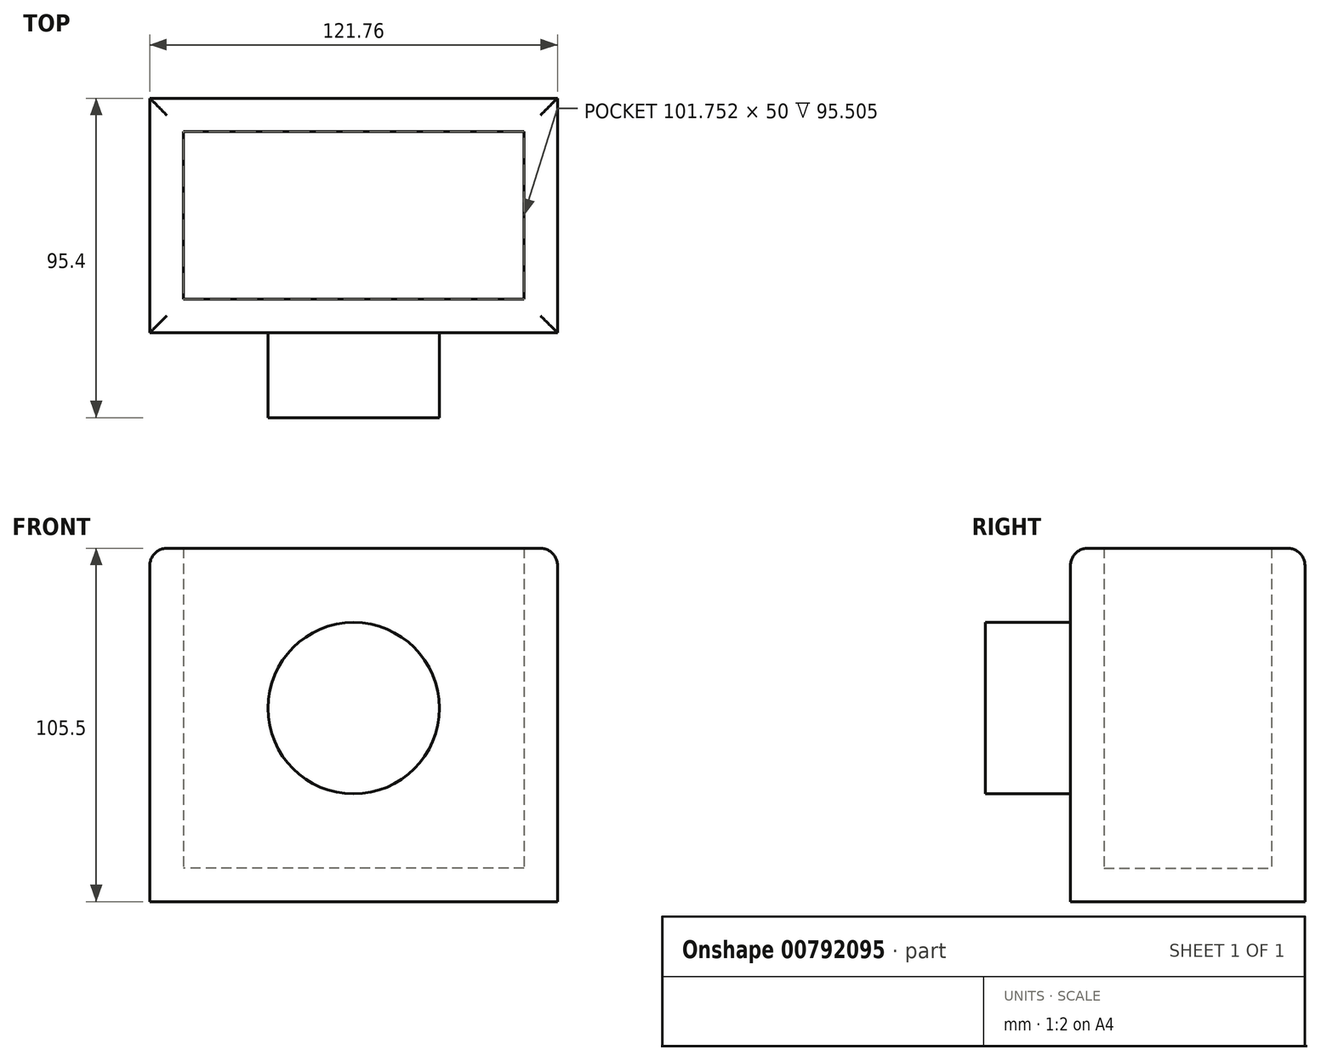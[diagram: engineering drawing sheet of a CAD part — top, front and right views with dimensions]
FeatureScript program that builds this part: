
annotation { "Feature Type Name" : "Feature", "Feature Type Description" : "" }
export const myFeature = defineFeature(function(context is Context, id is Id, definition is map)
    precondition{}
    {
        {
            var Q0;
            Q0=qCreatedBy(makeId("Front.planeOp"),FACE);
            var sketch = newSketch(context, id + "F0", { "sketchPlane" : qUnion([Q0])});
            skLineSegment(sketch, "E0.bottom", {"start": v(50.88, 47.75) * mm, "end": v(-50.88, 47.75) * mm});
            skLineSegment(sketch, "E0.top", {"start": v(50.88, -47.75) * mm, "end": v(-50.88, -47.75) * mm});
            skLineSegment(sketch, "E0.left", {"start": v(50.88, 47.75) * mm, "end": v(50.88, -47.75) * mm});
            skLineSegment(sketch, "E0.right", {"start": v(-50.88, 47.75) * mm, "end": v(-50.88, -47.75) * mm});
            skPoint(sketch, "E0.middle", {"position": v(0, 0) * mm});
            skSolve(sketch);
        }
        {
            var Q0;
            Q0=makeQuery(id+"F0.imprint","IMPRINT",FACE,{"disambiguationData":[TD([[makeQuery(id+"F0.imprint","IMPRINT",EDGE,{"derivedFrom":sQuery(id+"F0.wireOp",EDGE,"E0.bottom")}),1.0]])]});
            extrude(context, id + "F1", {"entities" : qUnion([Q0]), "endBound" : BoundingType.SYMMETRIC, "depth" : 50 * mm, "offsetDistance" : 25.4 * mm});
        }
        {
            var Q0;
            Q0=makeQuery(id+"F1.opExtrude","SWEPT_FACE",FACE,{"disambiguationData":[OSD([sQuery(id+"F0.wireOp",EDGE,"E0.bottom")])]});
            shell(context, id + "F2", {"entities" : qUnion([Q0]), "thickness" : 10 * mm, "oppositeDirection" : true});
        }
        {
            var Q0;
            Q0=makeQuery(id+"F1.opExtrude","CAP_FACE",FACE,{"disambiguationData":[OSD([sQuery(id+"F0.wireOp",EDGE,"E0.bottom"),sQuery(id+"F0.wireOp",EDGE,"E0.top"),sQuery(id+"F0.wireOp",EDGE,"E0.left"),sQuery(id+"F0.wireOp",EDGE,"E0.right")])],"isStart":false});
            var sketch = newSketch(context, id + "F3", { "sketchPlane" : qUnion([Q0])});
            skCircle(sketch, "E1", {"center": v(0, 0) * mm, "radius": 25.6 * mm});
            skSolve(sketch);
        }
        {
            var Q0;
            Q0=makeQuery(id+"F3.imprint","IMPRINT",FACE,{"disambiguationData":[TD([[makeQuery(id+"F3.imprint","IMPRINT",EDGE,{"derivedFrom":sQuery(id+"F3.wireOp",EDGE,"E1")}),1.0]])]});
            extrude(context, id + "F4", {"entities" : qUnion([Q0]), "operationType" : NewBodyOperationType.ADD, "depth" : 25.4 * mm, "offsetDistance" : 25.4 * mm});
        }
        {
            var Q0;
            Q0=makeQuery(id+"F1.opExtrude","CAP_EDGE",EDGE,{"disambiguationData":[OSD([sQuery(id+"F0.wireOp",EDGE,"E0.bottom")])],"isStart":false});
            var Q1;
            Q1=makeQuery(id+"F1.opExtrude","SWEPT_EDGE",EDGE,{"disambiguationData":[OSD([sQuery(id+"F0.wireOp",EDGE,"E0.bottom"),sQuery(id+"F0.wireOp",EDGE,"E0.left")])]});
            var Q2;
            Q2=makeQuery(id+"F1.opExtrude","CAP_EDGE",EDGE,{"disambiguationData":[OSD([sQuery(id+"F0.wireOp",EDGE,"E0.bottom")])],"isStart":true});
            var Q3;
            Q3=makeQuery(id+"F1.opExtrude","SWEPT_EDGE",EDGE,{"disambiguationData":[OSD([sQuery(id+"F0.wireOp",EDGE,"E0.bottom"),sQuery(id+"F0.wireOp",EDGE,"E0.right")])]});
            fillet(context, id + "F5", {"entities" : qUnion([Q0, Q1, Q2, Q3]), "radius" : 5.08 * mm, "tangentPropagation" : true, "allowEdgeOverflow" : false});
        }
    });
